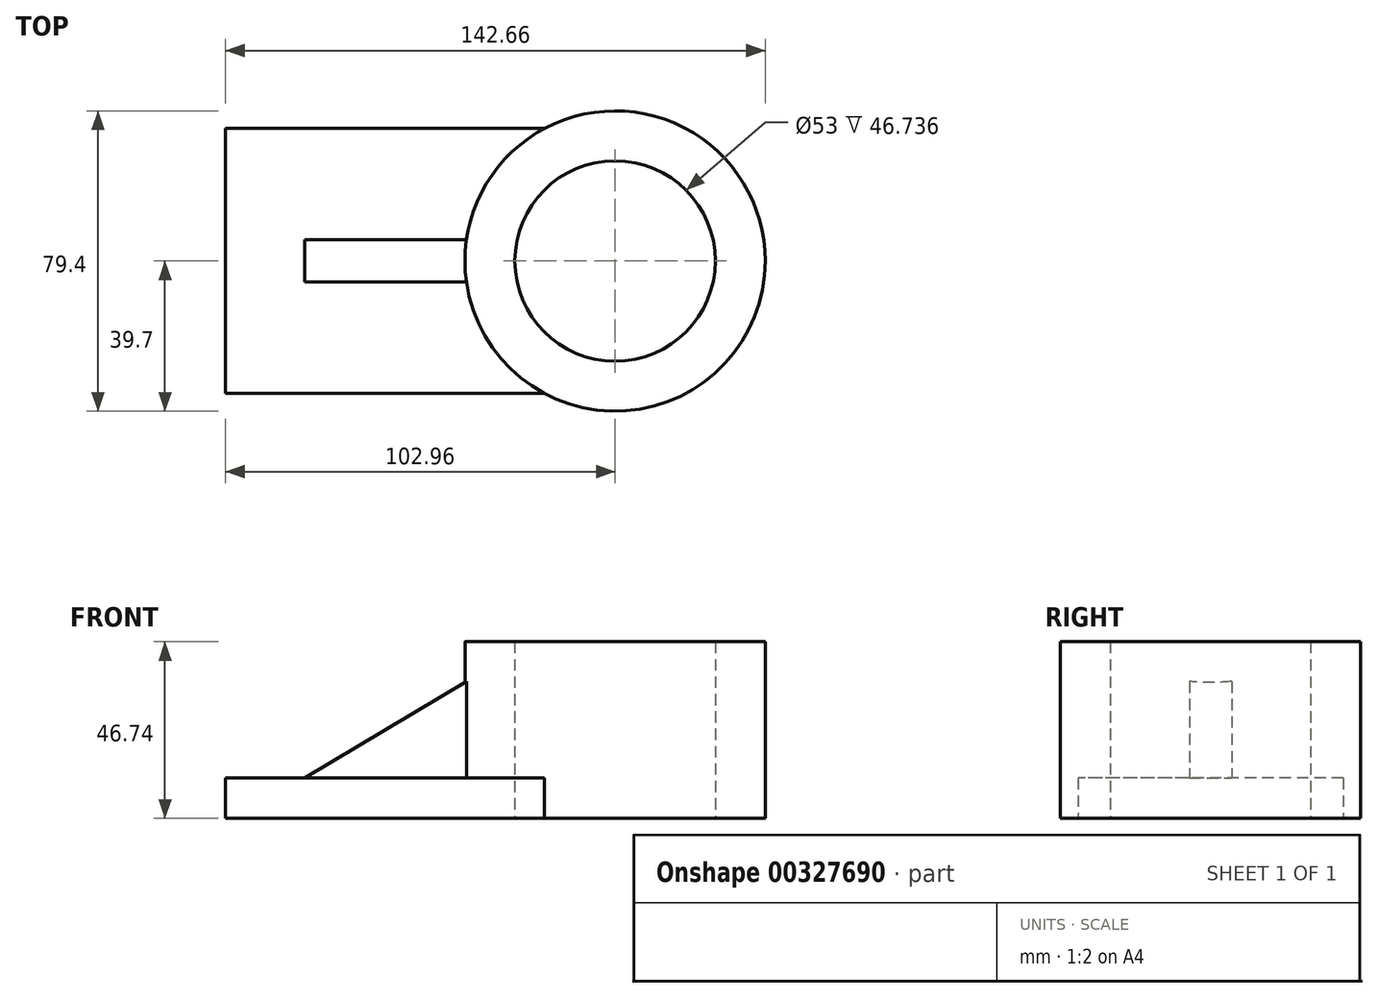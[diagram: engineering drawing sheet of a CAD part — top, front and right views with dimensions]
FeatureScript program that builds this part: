
annotation { "Feature Type Name" : "Feature", "Feature Type Description" : "" }
export const myFeature = defineFeature(function(context is Context, id is Id, definition is map)
    precondition{}
    {
        {
            var Q0;
            Q0=qCreatedBy(makeId("Top.planeOp"),FACE);
            var sketch = newSketch(context, id + "F0", { "sketchPlane" : qUnion([Q0])});
            skCircle(sketch, "E0", {"center": v(39.7, 0) * mm, "radius": 39.7 * mm});
            skCircle(sketch, "E1", {"center": v(39.7, 0) * mm, "radius": 26.5 * mm});
            skSolve(sketch);
        }
        {
            var Q0;
            Q0 = qSketchRegion(id + "F0", true);
            var Q1;
            Q1=makeQuery(id+"F0.imprint","IMPRINT",FACE,{"disambiguationData":[TD([[makeQuery(id+"F0.imprint","IMPRINT",EDGE,{"derivedFrom":sQuery(id+"F0.wireOp",EDGE,"E0")}),1.0]])]});
            extrude(context, id + "F1", {"entities" : qUnion([Q0, Q1]), "depth" : 46.74 * mm});
        }
        {
            var Q0;
            Q0=makeQuery(id+"F1.opExtrude","CAP_FACE",FACE,{"disambiguationData":[OSD([sQuery(id+"F0.wireOp",EDGE,"E0"),sQuery(id+"F0.wireOp",EDGE,"E1")])],"isStart":true});
            var sketch = newSketch(context, id + "F2", { "sketchPlane" : qUnion([Q0])});
            skLineSegment(sketch, "E2.bottom", {"start": v(21.05, -35.05) * mm, "end": v(-63.26, -35.05) * mm});
            skLineSegment(sketch, "E2.top", {"start": v(21.05, 35.05) * mm, "end": v(-63.26, 35.05) * mm});
            skLineSegment(sketch, "E2.left", {"start": v(21.05, -35.05) * mm, "end": v(21.05, 35.05) * mm});
            skLineSegment(sketch, "E2.right", {"start": v(-63.26, -35.05) * mm, "end": v(-63.26, 35.05) * mm});
            skPoint(sketch, "E2.middle", {"position": v(-21.1, 0) * mm});
            skSolve(sketch);
        }
        {
            var Q0;
            {var subQ0=sQuery(id+"F2.wireOp",EDGE,"E2.bottom");Q0=makeQuery(id+"F2.imprint","IMPRINT",FACE,{"disambiguationData":[TD([[makeQuery(id+"F2.imprint","IMPRINT",EDGE,{"derivedFrom":subQ0}),-1.0]])]});}
            extrude(context, id + "F3", {"entities" : qUnion([Q0]), "operationType" : NewBodyOperationType.ADD, "oppositeDirection" : true, "depth" : 10.67 * mm});
        }
        {
            var Q0;
            Q0=qCreatedBy(makeId("Front.planeOp"),FACE);
            var sketch = newSketch(context, id + "F4", { "sketchPlane" : qUnion([Q0])});
            skLineSegment(sketch, "E3", {"start": v(-47.92, 7.36) * mm, "end": v(4.87, 38.9) * mm});
            skLineSegment(sketch, "E4", {"start": v(4.87, 38.9) * mm, "end": v(4.87, 6.66) * mm});
            skLineSegment(sketch, "E5", {"start": v(4.87, 6.66) * mm, "end": v(-47.92, 7.36) * mm});
            skSolve(sketch);
        }
        {
            var Q0;
            Q0 = qSketchRegion(id + "F4", true);
            extrude(context, id + "F5", {"entities" : qUnion([Q0]), "operationType" : NewBodyOperationType.ADD, "endBound" : BoundingType.SYMMETRIC, "depth" : 11.18 * mm});
        }
    });
